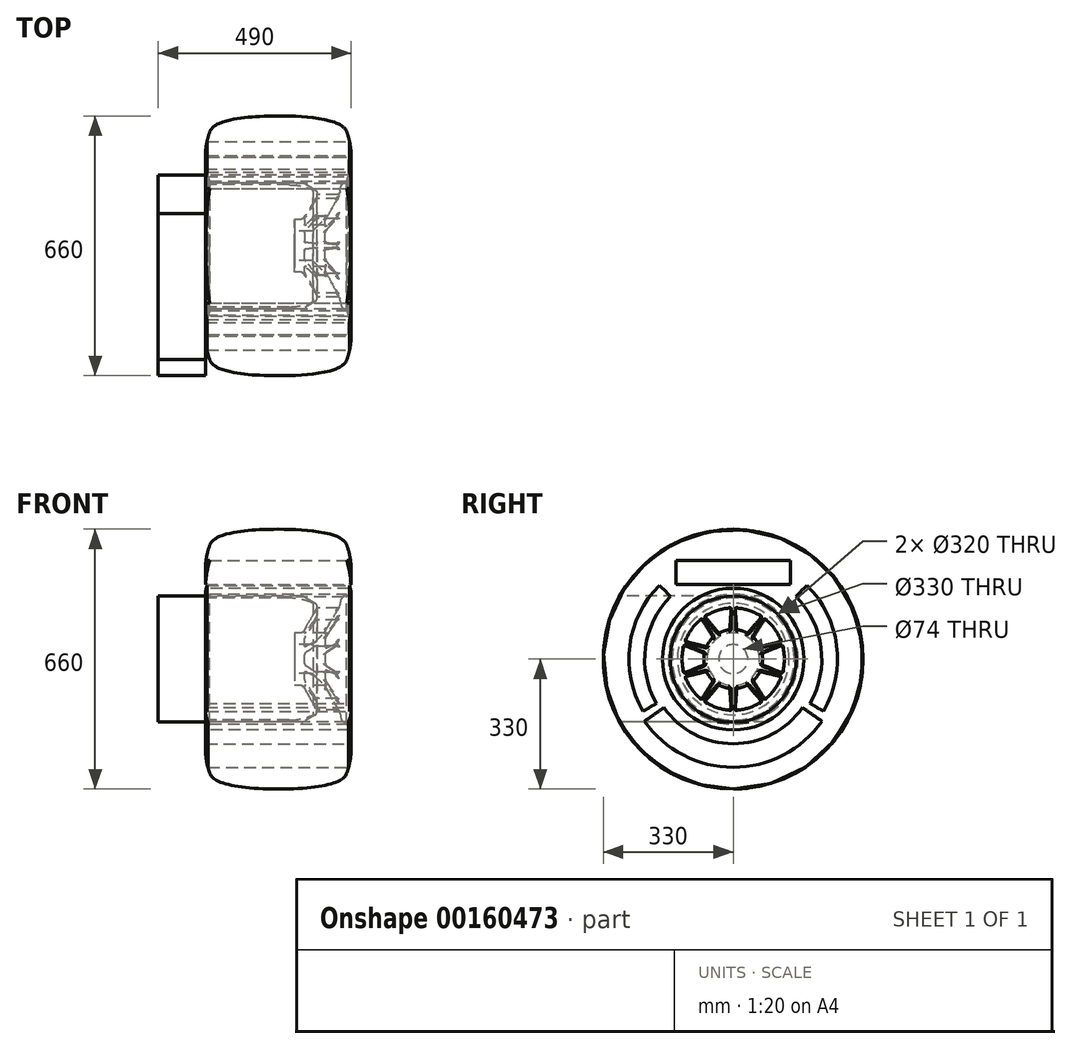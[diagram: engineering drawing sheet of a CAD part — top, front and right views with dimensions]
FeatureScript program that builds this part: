
annotation { "Feature Type Name" : "Feature", "Feature Type Description" : "" }
export const myFeature = defineFeature(function(context is Context, id is Id, definition is map)
    precondition{}
    {
        {
            var Q0;
            Q0=qCreatedBy(makeId("Front.planeOp"),FACE);
            var sketch = newSketch(context, id + "F0", { "sketchPlane" : qUnion([Q0])});
            skLineSegment(sketch, "E0.bottom", {"start": v(0, 0) * mm, "end": v(-190, 0) * mm, "construction": true});
            skLineSegment(sketch, "E0.top", {"start": v(0, 340) * mm, "end": v(-190, 340) * mm, "construction": true});
            skLineSegment(sketch, "E0.left", {"start": v(0, 0) * mm, "end": v(0, 340) * mm, "construction": true});
            skLineSegment(sketch, "E0.right", {"start": v(-190, 0) * mm, "end": v(-190, 340) * mm, "construction": true});
            skLineSegment(sketch, "E1", {"start": v(0, 165) * mm, "end": v(-174, 165) * mm});
            skEllipticalArc(sketch, "E2", {});
            skLineSegment(sketch, "E3", {"start": v(0, 330) * mm, "end": v(-190, 330) * mm, "construction": true});
            skLineSegment(sketch, "E4", {"start": v(-174, 165) * mm, "end": v(-174, 290) * mm, "construction": true});
            skEllipticalArc(sketch, "E5", {});
            skLineSegment(sketch, "E6", {"start": v(-185, 227.5) * mm, "end": v(-174, 227.5) * mm, "construction": true});
            skLineSegment(sketch, "E7.MirrorCS", {"start": v(0, 165) * mm, "end": v(174, 165) * mm});
            skEllipticalArc(sketch, "E8.MirrorCS", {});
            skEllipticalArc(sketch, "E9.MirrorCS", {});
            skLineSegment(sketch, "E10", {"start": v(-185, 227.5) * mm, "end": v(-185, 0) * mm, "construction": true});
            skLineSegment(sketch, "E11.MirrorCS", {"start": v(190, 0) * mm, "end": v(190, 340) * mm, "construction": true});
            skLineSegment(sketch, "E12.MirrorCS", {"start": v(0, 340) * mm, "end": v(190, 340) * mm, "construction": true});
            skLineSegment(sketch, "E13.MirrorCS", {"start": v(0, 0) * mm, "end": v(190, 0) * mm, "construction": true});
            const initialGuessF0  = {"E2": [0.9520342089782073, 0.02400839074373489, 0.9737164487381573, -0.22776364384324302, 1.1571666407658359, 0.15965277178562093, 2.608682838389242, 3.1257403974799214], "E5": [0.126, 0.2275, -1, 0, 0.311, 0.23709558046524198, 6.0164259862504625, 0.2667593209291309], "E8.MirrorCS": [-0.126, 0.2275, 1, 0, 0.311, 0.23709558046524198, 6.016425986250454, 0.2667593209291219], "E9.MirrorCS": [-0.9520342089782073, 0.02400839074373489, -0.9737164487381573, -0.22776364384324302, 1.1571666407658359, 0.15965277178562093, 3.1574449096996635, 3.6745024687903425]};
            skSetInitialGuess(sketch, initialGuessF0);
            skSolve(sketch);
        }
        {
            var Q0;
            Q0=qCreatedBy(makeId("Right.planeOp"),FACE);
            var sketch = newSketch(context, id + "F1", { "sketchPlane" : qUnion([Q0])});
            skLineSegment(sketch, "E14", {"start": v(0, 190) * mm, "end": v(0, -215) * mm, "construction": true});
            skLineSegment(sketch, "E15.bottom", {"start": v(0, 190) * mm, "end": v(-145, 190) * mm});
            skLineSegment(sketch, "E15.top", {"start": v(0, 250) * mm, "end": v(-145, 250) * mm});
            skLineSegment(sketch, "E15.left", {"start": v(0, 190) * mm, "end": v(0, 250) * mm});
            skLineSegment(sketch, "E15.right", {"start": v(-145, 190) * mm, "end": v(-145, 250) * mm});
            skArc(sketch, "E16", {"start": v(-159.1, 159.1) * mm, "mid": v(-223.08, 29.37) * mm, "end": v(-194.86, -112.5) * mm});
            skArc(sketch, "E17", {"start": v(-187.38, 187.38) * mm, "mid": v(-262.73, 34.59) * mm, "end": v(-229.5, -132.5) * mm});
            skLineSegment(sketch, "E18", {"start": v(-159.1, 159.1) * mm, "end": v(-187.38, 187.38) * mm});
            skLineSegment(sketch, "E19", {"start": v(-194.86, -112.5) * mm, "end": v(-229.5, -132.5) * mm});
            skArc(sketch, "E20", {"start": v(-176.12, -123.32) * mm, "mid": v(-99.28, -190.7) * mm, "end": v(0, -215) * mm});
            skArc(sketch, "E21", {"start": v(-225.27, -157.73) * mm, "mid": v(-126.98, -243.93) * mm, "end": v(0, -275) * mm});
            skLineSegment(sketch, "E22", {"start": v(-176.12, -123.32) * mm, "end": v(-225.27, -157.73) * mm});
            skLineSegment(sketch, "E23", {"start": v(0, -215) * mm, "end": v(0, -275) * mm});
            skLineSegment(sketch, "E24.MirrorCS", {"start": v(0, 250) * mm, "end": v(145, 250) * mm});
            skLineSegment(sketch, "E25.MirrorCS", {"start": v(145, 190) * mm, "end": v(145, 250) * mm});
            skLineSegment(sketch, "E26.MirrorCS", {"start": v(0, 190) * mm, "end": v(145, 190) * mm});
            skLineSegment(sketch, "E27.MirrorCS", {"start": v(159.1, 159.1) * mm, "end": v(187.38, 187.38) * mm});
            skArc(sketch, "E28.MirrorCS", {"start": v(187.38, 187.38) * mm, "mid": v(262.73, 34.59) * mm, "end": v(229.5, -132.5) * mm});
            skArc(sketch, "E29.MirrorCS", {"start": v(159.1, 159.1) * mm, "mid": v(223.08, 29.37) * mm, "end": v(194.86, -112.5) * mm});
            skLineSegment(sketch, "E30.MirrorCS", {"start": v(194.86, -112.5) * mm, "end": v(229.5, -132.5) * mm});
            skLineSegment(sketch, "E31.MirrorCS", {"start": v(176.12, -123.32) * mm, "end": v(225.27, -157.73) * mm});
            skArc(sketch, "E32.MirrorCS", {"start": v(225.27, -157.73) * mm, "mid": v(126.98, -243.93) * mm, "end": v(0, -275) * mm});
            skArc(sketch, "E33.MirrorCS", {"start": v(176.12, -123.32) * mm, "mid": v(99.28, -190.7) * mm, "end": v(0, -215) * mm});
            skSolve(sketch);
        }
        {
            var Q0;
            Q0=qCreatedBy(makeId("Front.planeOp"),FACE);
            var sketch = newSketch(context, id + "F2", { "sketchPlane" : qUnion([Q0])});
            skLineSegment(sketch, "E34.bottom", {"start": v(-180, 180) * mm, "end": v(180, 180) * mm});
            skLineSegment(sketch, "E34.top", {"start": v(-180, 160) * mm, "end": v(59.32, 160) * mm});
            skLineSegment(sketch, "E34.left", {"start": v(-185, 175) * mm, "end": v(-185, 165) * mm});
            skLineSegment(sketch, "E34.right", {"start": v(185, 175) * mm, "end": v(185, 165) * mm});
            skPoint(sketch, "E35.visualSharp", {"position": v(-185, 160) * mm});
            skArc(sketch, "E35.filletArc", {"start": v(-185, 165) * mm, "mid": v(-183.54, 161.46) * mm, "end": v(-180, 160) * mm});
            skPoint(sketch, "E36.visualSharp", {"position": v(185, 160) * mm});
            skArc(sketch, "E36.filletArc", {"start": v(180, 160) * mm, "mid": v(183.54, 161.46) * mm, "end": v(185, 165) * mm});
            skPoint(sketch, "E37.visualSharp", {"position": v(185, 180) * mm});
            skArc(sketch, "E37.filletArc", {"start": v(185, 175) * mm, "mid": v(183.54, 178.54) * mm, "end": v(180, 180) * mm});
            skPoint(sketch, "E38.visualSharp", {"position": v(-185, 180) * mm});
            skArc(sketch, "E38.filletArc", {"start": v(-180, 180) * mm, "mid": v(-183.54, 178.54) * mm, "end": v(-185, 175) * mm});
            skLineSegment(sketch, "E39", {"start": v(82.86, 37) * mm, "end": v(42, 37) * mm});
            skLineSegment(sketch, "E40", {"start": v(42, 37) * mm, "end": v(42, 67) * mm});
            skLineSegment(sketch, "E41", {"start": v(42, 67) * mm, "end": v(56.23, 67) * mm});
            skLineSegment(sketch, "E42", {"start": v(64.89, 72) * mm, "end": v(97.27, 128.09) * mm});
            skLineSegment(sketch, "E43", {"start": v(93.6, 141.75) * mm, "end": v(64.32, 158.66) * mm});
            skLineSegment(sketch, "E44", {"start": v(89.93, 39.93) * mm, "end": v(116.07, 66.07) * mm});
            skLineSegment(sketch, "E45", {"start": v(117.66, 68.14) * mm, "end": v(156.39, 135.22) * mm});
            skLineSegment(sketch, "E46", {"start": v(157.58, 138.49) * mm, "end": v(159.91, 151.74) * mm});
            skLineSegment(sketch, "E47.trimOffspring", {"start": v(169.76, 160) * mm, "end": v(180, 160) * mm});
            skPoint(sketch, "E48.visualSharp", {"position": v(62, 160) * mm});
            skArc(sketch, "E48.filletArc", {"start": v(64.32, 158.66) * mm, "mid": v(61.9, 159.66) * mm, "end": v(59.32, 160) * mm});
            skPoint(sketch, "E49.visualSharp", {"position": v(62, 67) * mm});
            skArc(sketch, "E49.filletArc", {"start": v(56.23, 67) * mm, "mid": v(61.23, 68.34) * mm, "end": v(64.89, 72) * mm});
            skPoint(sketch, "E50.visualSharp", {"position": v(87, 37) * mm});
            skArc(sketch, "E50.filletArc", {"start": v(82.86, 37) * mm, "mid": v(86.68, 37.76) * mm, "end": v(89.93, 39.93) * mm});
            skPoint(sketch, "E51.visualSharp", {"position": v(117, 67) * mm});
            skArc(sketch, "E51.filletArc", {"start": v(116.07, 66.07) * mm, "mid": v(116.93, 67.05) * mm, "end": v(117.66, 68.14) * mm});
            skPoint(sketch, "E52.visualSharp", {"position": v(157.27, 136.75) * mm});
            skArc(sketch, "E52.filletArc", {"start": v(156.39, 135.22) * mm, "mid": v(157.13, 136.8) * mm, "end": v(157.58, 138.49) * mm});
            skPoint(sketch, "E53.visualSharp", {"position": v(161.37, 160) * mm});
            skArc(sketch, "E53.filletArc", {"start": v(169.76, 160) * mm, "mid": v(163.33, 157.66) * mm, "end": v(159.91, 151.74) * mm});
            skPoint(sketch, "E54.visualSharp", {"position": v(102.27, 136.75) * mm});
            skArc(sketch, "E54.filletArc", {"start": v(97.27, 128.09) * mm, "mid": v(98.27, 135.68) * mm, "end": v(93.6, 141.75) * mm});
            skSolve(sketch);
        }
        {
            var Q0;
            Q0=qCreatedBy(makeId("Right.planeOp"),FACE);
            var sketch = newSketch(context, id + "F3", { "sketchPlane" : qUnion([Q0])});
            skLineSegment(sketch, "E55", {"start": v(5.4, 124.22) * mm, "end": v(8.6, 78.49) * mm});
            skLineSegment(sketch, "E56", {"start": v(40.17, 123.64) * mm, "end": v(23.18, 71.33) * mm, "construction": true});
            skLineSegment(sketch, "E57", {"start": v(23.18, 71.33) * mm, "end": v(0, 0) * mm, "construction": true});
            skArc(sketch, "E58", {"start": v(23.18, 71.33) * mm, "mid": v(18, 72.8) * mm, "end": v(12.73, 73.91) * mm});
            skArc(sketch, "E59", {"start": v(40.17, 123.64) * mm, "mid": v(25.66, 127.44) * mm, "end": v(10.8, 129.55) * mm});
            skArc(sketch, "E60.MirrorCS", {"start": v(23.18, 71.33) * mm, "mid": v(28.23, 69.48) * mm, "end": v(33.14, 67.28) * mm});
            skLineSegment(sketch, "E61.MirrorCS", {"start": v(68.65, 103.67) * mm, "end": v(39.18, 68.55) * mm});
            skArc(sketch, "E62.MirrorCS", {"start": v(40.17, 123.64) * mm, "mid": v(54.15, 118.18) * mm, "end": v(67.4, 111.16) * mm});
            skPoint(sketch, "E63.visualSharp", {"position": v(8.88, 74.47) * mm});
            skArc(sketch, "E63.filletArc", {"start": v(8.6, 78.49) * mm, "mid": v(9.87, 75.49) * mm, "end": v(12.73, 73.91) * mm});
            skPoint(sketch, "E64.visualSharp", {"position": v(5, 129.9) * mm});
            skArc(sketch, "E64.filletArc", {"start": v(10.8, 129.55) * mm, "mid": v(6.87, 128.13) * mm, "end": v(5.4, 124.22) * mm});
            skPoint(sketch, "E65.visualSharp", {"position": v(36.6, 65.47) * mm});
            skArc(sketch, "E65.filletArc", {"start": v(33.14, 67.28) * mm, "mid": v(36.38, 66.87) * mm, "end": v(39.18, 68.55) * mm});
            skPoint(sketch, "E66.visualSharp", {"position": v(72.31, 108.03) * mm});
            skArc(sketch, "E66.filletArc", {"start": v(68.65, 103.67) * mm, "mid": v(69.75, 107.7) * mm, "end": v(67.4, 111.16) * mm});
            skLineSegment(sketch, "E67.1.0", {"start": v(-5.4, 124.22) * mm, "end": v(-8.6, 78.49) * mm});
            skArc(sketch, "E67.1.1", {"start": v(-5.4, 124.22) * mm, "mid": v(-6.87, 128.13) * mm, "end": v(-10.8, 129.55) * mm});
            skArc(sketch, "E67.1.2", {"start": v(-40.17, 123.64) * mm, "mid": v(-25.66, 127.44) * mm, "end": v(-10.8, 129.55) * mm});
            skArc(sketch, "E67.1.3", {"start": v(-40.17, 123.64) * mm, "mid": v(-54.15, 118.18) * mm, "end": v(-67.4, 111.16) * mm});
            skArc(sketch, "E67.1.4", {"start": v(-67.4, 111.16) * mm, "mid": v(-69.75, 107.7) * mm, "end": v(-68.65, 103.67) * mm});
            skLineSegment(sketch, "E67.1.5", {"start": v(-68.65, 103.67) * mm, "end": v(-39.18, 68.55) * mm});
            skArc(sketch, "E67.1.6", {"start": v(-39.18, 68.55) * mm, "mid": v(-36.38, 66.87) * mm, "end": v(-33.14, 67.28) * mm});
            skArc(sketch, "E67.1.7", {"start": v(-23.18, 71.33) * mm, "mid": v(-28.23, 69.48) * mm, "end": v(-33.14, 67.28) * mm});
            skArc(sketch, "E67.1.8", {"start": v(-23.18, 71.33) * mm, "mid": v(-18, 72.8) * mm, "end": v(-12.73, 73.91) * mm});
            skArc(sketch, "E67.1.9", {"start": v(-12.73, 73.91) * mm, "mid": v(-9.87, 75.49) * mm, "end": v(-8.6, 78.49) * mm});
            skLineSegment(sketch, "E67.2.0", {"start": v(-77.38, 97.32) * mm, "end": v(-53.09, 58.45) * mm});
            skArc(sketch, "E67.2.1", {"start": v(-77.38, 97.32) * mm, "mid": v(-80.87, 99.62) * mm, "end": v(-84.89, 98.46) * mm});
            skArc(sketch, "E67.2.2", {"start": v(-105.17, 76.41) * mm, "mid": v(-95.67, 88.02) * mm, "end": v(-84.89, 98.46) * mm});
            skArc(sketch, "E67.2.3", {"start": v(-105.17, 76.41) * mm, "mid": v(-113.28, 63.78) * mm, "end": v(-119.87, 50.3) * mm});
            skArc(sketch, "E67.2.4", {"start": v(-119.87, 50.3) * mm, "mid": v(-119.73, 46.13) * mm, "end": v(-116.47, 43.52) * mm});
            skLineSegment(sketch, "E67.2.5", {"start": v(-116.47, 43.52) * mm, "end": v(-72, 32.43) * mm});
            skArc(sketch, "E67.2.6", {"start": v(-72, 32.43) * mm, "mid": v(-68.74, 32.72) * mm, "end": v(-66.36, 34.95) * mm});
            skArc(sketch, "E67.2.7", {"start": v(-60.68, 44.08) * mm, "mid": v(-63.68, 39.62) * mm, "end": v(-66.36, 34.95) * mm});
            skArc(sketch, "E67.2.8", {"start": v(-60.68, 44.08) * mm, "mid": v(-57.36, 48.32) * mm, "end": v(-53.75, 52.31) * mm});
            skArc(sketch, "E67.2.9", {"start": v(-53.75, 52.31) * mm, "mid": v(-52.36, 55.27) * mm, "end": v(-53.09, 58.45) * mm});
            skLineSegment(sketch, "E67.3.0", {"start": v(-119.8, 33.25) * mm, "end": v(-77.3, 16.08) * mm});
            skArc(sketch, "E67.3.1", {"start": v(-119.8, 33.25) * mm, "mid": v(-123.98, 33.06) * mm, "end": v(-126.55, 29.76) * mm});
            skArc(sketch, "E67.3.2", {"start": v(-130, 0) * mm, "mid": v(-129.13, 14.98) * mm, "end": v(-126.55, 29.76) * mm});
            skArc(sketch, "E67.3.3", {"start": v(-130, 0) * mm, "mid": v(-129.13, -14.98) * mm, "end": v(-126.55, -29.76) * mm});
            skArc(sketch, "E67.3.4", {"start": v(-126.55, -29.76) * mm, "mid": v(-123.98, -33.06) * mm, "end": v(-119.8, -33.25) * mm});
            skLineSegment(sketch, "E67.3.5", {"start": v(-119.8, -33.25) * mm, "end": v(-77.3, -16.08) * mm});
            skArc(sketch, "E67.3.6", {"start": v(-77.3, -16.08) * mm, "mid": v(-74.84, -13.94) * mm, "end": v(-74.23, -10.73) * mm});
            skArc(sketch, "E67.3.7", {"start": v(-75, 0) * mm, "mid": v(-74.8, -5.38) * mm, "end": v(-74.23, -10.73) * mm});
            skArc(sketch, "E67.3.8", {"start": v(-75, 0) * mm, "mid": v(-74.8, 5.38) * mm, "end": v(-74.23, 10.73) * mm});
            skArc(sketch, "E67.3.9", {"start": v(-74.23, 10.73) * mm, "mid": v(-74.84, 13.94) * mm, "end": v(-77.3, 16.08) * mm});
            skLineSegment(sketch, "E67.4.0", {"start": v(-116.47, -43.52) * mm, "end": v(-72, -32.43) * mm});
            skArc(sketch, "E67.4.1", {"start": v(-116.47, -43.52) * mm, "mid": v(-119.73, -46.13) * mm, "end": v(-119.87, -50.3) * mm});
            skArc(sketch, "E67.4.2", {"start": v(-105.17, -76.41) * mm, "mid": v(-113.28, -63.78) * mm, "end": v(-119.87, -50.3) * mm});
            skArc(sketch, "E67.4.3", {"start": v(-105.17, -76.41) * mm, "mid": v(-95.67, -88.02) * mm, "end": v(-84.89, -98.46) * mm});
            skArc(sketch, "E67.4.4", {"start": v(-84.89, -98.46) * mm, "mid": v(-80.87, -99.62) * mm, "end": v(-77.38, -97.32) * mm});
            skLineSegment(sketch, "E67.4.5", {"start": v(-77.38, -97.32) * mm, "end": v(-53.09, -58.45) * mm});
            skArc(sketch, "E67.4.6", {"start": v(-53.09, -58.45) * mm, "mid": v(-52.36, -55.27) * mm, "end": v(-53.75, -52.31) * mm});
            skArc(sketch, "E67.4.7", {"start": v(-60.68, -44.08) * mm, "mid": v(-57.36, -48.32) * mm, "end": v(-53.75, -52.31) * mm});
            skArc(sketch, "E67.4.8", {"start": v(-60.68, -44.08) * mm, "mid": v(-63.68, -39.62) * mm, "end": v(-66.36, -34.95) * mm});
            skArc(sketch, "E67.4.9", {"start": v(-66.36, -34.95) * mm, "mid": v(-68.74, -32.72) * mm, "end": v(-72, -32.43) * mm});
            skLineSegment(sketch, "E67.5.0", {"start": v(-68.65, -103.67) * mm, "end": v(-39.18, -68.55) * mm});
            skArc(sketch, "E67.5.1", {"start": v(-68.65, -103.67) * mm, "mid": v(-69.75, -107.7) * mm, "end": v(-67.4, -111.16) * mm});
            skArc(sketch, "E67.5.2", {"start": v(-40.17, -123.64) * mm, "mid": v(-54.15, -118.18) * mm, "end": v(-67.4, -111.16) * mm});
            skArc(sketch, "E67.5.3", {"start": v(-40.17, -123.64) * mm, "mid": v(-25.66, -127.44) * mm, "end": v(-10.8, -129.55) * mm});
            skArc(sketch, "E67.5.4", {"start": v(-10.8, -129.55) * mm, "mid": v(-6.87, -128.13) * mm, "end": v(-5.4, -124.22) * mm});
            skLineSegment(sketch, "E67.5.5", {"start": v(-5.4, -124.22) * mm, "end": v(-8.6, -78.49) * mm});
            skArc(sketch, "E67.5.6", {"start": v(-8.6, -78.49) * mm, "mid": v(-9.87, -75.49) * mm, "end": v(-12.73, -73.91) * mm});
            skArc(sketch, "E67.5.7", {"start": v(-23.18, -71.33) * mm, "mid": v(-18, -72.8) * mm, "end": v(-12.73, -73.91) * mm});
            skArc(sketch, "E67.5.8", {"start": v(-23.18, -71.33) * mm, "mid": v(-28.23, -69.48) * mm, "end": v(-33.14, -67.28) * mm});
            skArc(sketch, "E67.5.9", {"start": v(-33.14, -67.28) * mm, "mid": v(-36.38, -66.87) * mm, "end": v(-39.18, -68.55) * mm});
            skLineSegment(sketch, "E67.6.0", {"start": v(5.4, -124.22) * mm, "end": v(8.6, -78.49) * mm});
            skArc(sketch, "E67.6.1", {"start": v(5.4, -124.22) * mm, "mid": v(6.87, -128.13) * mm, "end": v(10.8, -129.55) * mm});
            skArc(sketch, "E67.6.2", {"start": v(40.17, -123.64) * mm, "mid": v(25.66, -127.44) * mm, "end": v(10.8, -129.55) * mm});
            skArc(sketch, "E67.6.3", {"start": v(40.17, -123.64) * mm, "mid": v(54.15, -118.18) * mm, "end": v(67.4, -111.16) * mm});
            skArc(sketch, "E67.6.4", {"start": v(67.4, -111.16) * mm, "mid": v(69.75, -107.7) * mm, "end": v(68.65, -103.67) * mm});
            skLineSegment(sketch, "E67.6.5", {"start": v(68.65, -103.67) * mm, "end": v(39.18, -68.55) * mm});
            skArc(sketch, "E67.6.6", {"start": v(39.18, -68.55) * mm, "mid": v(36.38, -66.87) * mm, "end": v(33.14, -67.28) * mm});
            skArc(sketch, "E67.6.7", {"start": v(23.18, -71.33) * mm, "mid": v(28.23, -69.48) * mm, "end": v(33.14, -67.28) * mm});
            skArc(sketch, "E67.6.8", {"start": v(23.18, -71.33) * mm, "mid": v(18, -72.8) * mm, "end": v(12.73, -73.91) * mm});
            skArc(sketch, "E67.6.9", {"start": v(12.73, -73.91) * mm, "mid": v(9.87, -75.49) * mm, "end": v(8.6, -78.49) * mm});
            skLineSegment(sketch, "E67.7.0", {"start": v(77.38, -97.32) * mm, "end": v(53.09, -58.45) * mm});
            skArc(sketch, "E67.7.1", {"start": v(77.38, -97.32) * mm, "mid": v(80.87, -99.62) * mm, "end": v(84.89, -98.46) * mm});
            skArc(sketch, "E67.7.2", {"start": v(105.17, -76.41) * mm, "mid": v(95.67, -88.02) * mm, "end": v(84.89, -98.46) * mm});
            skArc(sketch, "E67.7.3", {"start": v(105.17, -76.41) * mm, "mid": v(113.28, -63.78) * mm, "end": v(119.87, -50.3) * mm});
            skArc(sketch, "E67.7.4", {"start": v(119.87, -50.3) * mm, "mid": v(119.73, -46.13) * mm, "end": v(116.47, -43.52) * mm});
            skLineSegment(sketch, "E67.7.5", {"start": v(116.47, -43.52) * mm, "end": v(72, -32.43) * mm});
            skArc(sketch, "E67.7.6", {"start": v(72, -32.43) * mm, "mid": v(68.74, -32.72) * mm, "end": v(66.36, -34.95) * mm});
            skArc(sketch, "E67.7.7", {"start": v(60.68, -44.08) * mm, "mid": v(63.68, -39.62) * mm, "end": v(66.36, -34.95) * mm});
            skArc(sketch, "E67.7.8", {"start": v(60.68, -44.08) * mm, "mid": v(57.36, -48.32) * mm, "end": v(53.75, -52.31) * mm});
            skArc(sketch, "E67.7.9", {"start": v(53.75, -52.31) * mm, "mid": v(52.36, -55.27) * mm, "end": v(53.09, -58.45) * mm});
            skLineSegment(sketch, "E67.8.0", {"start": v(119.8, -33.25) * mm, "end": v(77.3, -16.08) * mm});
            skArc(sketch, "E67.8.1", {"start": v(119.8, -33.25) * mm, "mid": v(123.98, -33.06) * mm, "end": v(126.55, -29.76) * mm});
            skArc(sketch, "E67.8.2", {"start": v(130, 0) * mm, "mid": v(129.13, -14.98) * mm, "end": v(126.55, -29.76) * mm});
            skArc(sketch, "E67.8.3", {"start": v(130, 0) * mm, "mid": v(129.13, 14.98) * mm, "end": v(126.55, 29.76) * mm});
            skArc(sketch, "E67.8.4", {"start": v(126.55, 29.76) * mm, "mid": v(123.98, 33.06) * mm, "end": v(119.8, 33.25) * mm});
            skLineSegment(sketch, "E67.8.5", {"start": v(119.8, 33.25) * mm, "end": v(77.3, 16.08) * mm});
            skArc(sketch, "E67.8.6", {"start": v(77.3, 16.08) * mm, "mid": v(74.84, 13.94) * mm, "end": v(74.23, 10.73) * mm});
            skArc(sketch, "E67.8.7", {"start": v(75, 0) * mm, "mid": v(74.8, 5.38) * mm, "end": v(74.23, 10.73) * mm});
            skArc(sketch, "E67.8.8", {"start": v(75, 0) * mm, "mid": v(74.8, -5.38) * mm, "end": v(74.23, -10.73) * mm});
            skArc(sketch, "E67.8.9", {"start": v(74.23, -10.73) * mm, "mid": v(74.84, -13.94) * mm, "end": v(77.3, -16.08) * mm});
            skLineSegment(sketch, "E67.9.0", {"start": v(116.47, 43.52) * mm, "end": v(72, 32.43) * mm});
            skArc(sketch, "E67.9.1", {"start": v(116.47, 43.52) * mm, "mid": v(119.73, 46.13) * mm, "end": v(119.87, 50.3) * mm});
            skArc(sketch, "E67.9.2", {"start": v(105.17, 76.41) * mm, "mid": v(113.28, 63.78) * mm, "end": v(119.87, 50.3) * mm});
            skArc(sketch, "E67.9.3", {"start": v(105.17, 76.41) * mm, "mid": v(95.67, 88.02) * mm, "end": v(84.89, 98.46) * mm});
            skArc(sketch, "E67.9.4", {"start": v(84.89, 98.46) * mm, "mid": v(80.87, 99.62) * mm, "end": v(77.38, 97.32) * mm});
            skLineSegment(sketch, "E67.9.5", {"start": v(77.38, 97.32) * mm, "end": v(53.09, 58.45) * mm});
            skArc(sketch, "E67.9.6", {"start": v(53.09, 58.45) * mm, "mid": v(52.36, 55.27) * mm, "end": v(53.75, 52.31) * mm});
            skArc(sketch, "E67.9.7", {"start": v(60.68, 44.08) * mm, "mid": v(57.36, 48.32) * mm, "end": v(53.75, 52.31) * mm});
            skArc(sketch, "E67.9.8", {"start": v(60.68, 44.08) * mm, "mid": v(63.68, 39.62) * mm, "end": v(66.36, 34.95) * mm});
            skArc(sketch, "E67.9.9", {"start": v(66.36, 34.95) * mm, "mid": v(68.74, 32.72) * mm, "end": v(72, 32.43) * mm});
            skSolve(sketch);
        }
        {
            var Q0;
            Q0=makeQuery(id+"F0.imprint","IMPRINT",FACE,{"disambiguationData":[TD([[makeQuery(id+"F0.imprint","IMPRINT",EDGE,{"derivedFrom":sQuery(id+"F0.wireOp",EDGE,"E1")}),-1.0]])]});
            var Q1;
            Q1=sQuery(id+"F0.wireOp",EDGE,"E0.bottom");
            revolve(context, id + "F4", {"entities" : qUnion([Q0]), "axis" : qUnion([Q1]), "revolveType" : RevolveType.FULL});
        }
        {
            var Q0;
            Q0=qSketchRegion(id+"F1",true);
            var Q1;
            Q1=makeQuery(id+"F4.opRevolve","SWEPT_FACE",FACE,{"disambiguationData":[OSD([sQuery(id+"F0.wireOp",EDGE,"E5")])]});
            extrude(context, id + "F5", {"entities" : qUnion([Q0]), "endBound" : BoundingType.UP_TO_NEXT, "oppositeDirection" : true, "depth" : 25 * mm, "hasSecondDirection" : true, "secondDirectionBound" : SecondDirectionBoundingType.UP_TO_NEXT, "secondDirectionOppositeDirection" : false, "secondDirectionBoundEntityFace" : qUnion([Q1]), "secondDirectionDepth" : 25 * mm});
        }
        {
            var Q0;
            Q0=makeQuery(id+"F5.opExtrude","SWEPT_BODY",BODY,{"disambiguationData":[OSD([sQuery(id+"F1.wireOp",EDGE,"E27.MirrorCS"),sQuery(id+"F1.wireOp",EDGE,"E28.MirrorCS"),sQuery(id+"F1.wireOp",EDGE,"E29.MirrorCS"),sQuery(id+"F1.wireOp",EDGE,"E30.MirrorCS")])]});
            var Q1;
            Q1=makeQuery(id+"F5.opExtrude","SWEPT_BODY",BODY,{"disambiguationData":[OSD([sQuery(id+"F1.wireOp",EDGE,"E15.bottom"),sQuery(id+"F1.wireOp",EDGE,"E15.top"),sQuery(id+"F1.wireOp",EDGE,"E15.right"),sQuery(id+"F1.wireOp",EDGE,"E24.MirrorCS"),sQuery(id+"F1.wireOp",EDGE,"E25.MirrorCS"),sQuery(id+"F1.wireOp",EDGE,"E26.MirrorCS")])]});
            var Q2;
            Q2=makeQuery(id+"F5.opExtrude","SWEPT_BODY",BODY,{"disambiguationData":[OSD([sQuery(id+"F1.wireOp",EDGE,"E16"),sQuery(id+"F1.wireOp",EDGE,"E17"),sQuery(id+"F1.wireOp",EDGE,"E18"),sQuery(id+"F1.wireOp",EDGE,"E19")])]});
            var Q3;
            Q3=makeQuery(id+"F5.opExtrude","SWEPT_BODY",BODY,{"disambiguationData":[OSD([sQuery(id+"F1.wireOp",EDGE,"E20"),sQuery(id+"F1.wireOp",EDGE,"E21"),sQuery(id+"F1.wireOp",EDGE,"E22"),sQuery(id+"F1.wireOp",EDGE,"E31.MirrorCS"),sQuery(id+"F1.wireOp",EDGE,"E32.MirrorCS"),sQuery(id+"F1.wireOp",EDGE,"E33.MirrorCS")])]});
            var Q4;
            Q4=makeQuery(id+"F4.opRevolve","SWEPT_BODY",BODY,{"disambiguationData":[OSD([sQuery(id+"F0.wireOp",EDGE,"E1"),sQuery(id+"F0.wireOp",EDGE,"E2"),sQuery(id+"F0.wireOp",EDGE,"E5"),sQuery(id+"F0.wireOp",EDGE,"E7.MirrorCS"),sQuery(id+"F0.wireOp",EDGE,"E8.MirrorCS"),sQuery(id+"F0.wireOp",EDGE,"E9.MirrorCS")])]});
            booleanBodies(context, id + "F6", {"operationType" : BooleanOperationType.SUBTRACTION, "tools" : qUnion([Q0, Q1, Q2, Q3]), "targets" : qUnion([Q4]), "keepTools" : true});
        }
        {
            var Q0;
            Q0=qSketchRegion(id+"F2",true);
            var Q1;
            Q1=sQuery(id+"F0.wireOp",EDGE,"E13.MirrorCS");
            revolve(context, id + "F7", {"entities" : qUnion([Q0]), "axis" : qUnion([Q1]), "revolveType" : RevolveType.FULL});
        }
        {
            var Q0;
            Q0=qSketchRegion(id+"F3",true);
            extrude(context, id + "F8", {"entities" : qUnion([Q0]), "operationType" : NewBodyOperationType.REMOVE, "endBound" : BoundingType.THROUGH_ALL, "depth" : 25 * mm});
        }
        {
            var Q0;
            Q0=makeQuery(id+"F8.boolean.opBoolean","INTERSECT",EDGE,{"derivedFrom":[makeQuery(id+"F7.opRevolve","SWEPT_FACE",FACE,{"disambiguationData":[OSD([sQuery(id+"F2.wireOp",EDGE,"E45")])]}),makeQuery(id+"F8.opExtrude","SWEPT_FACE",FACE,{"disambiguationData":[OSD([sQuery(id+"F3.wireOp",EDGE,"E67.1.5")])]})]});
            var Q1;
            Q1=makeQuery(id+"F8.boolean.opBoolean","INTERSECT",EDGE,{"derivedFrom":[makeQuery(id+"F7.opRevolve","SWEPT_FACE",FACE,{"disambiguationData":[OSD([sQuery(id+"F2.wireOp",EDGE,"E45")])]}),makeQuery(id+"F8.opExtrude","SWEPT_FACE",FACE,{"disambiguationData":[OSD([sQuery(id+"F3.wireOp",EDGE,"E55")])]})]});
            var Q2;
            Q2=makeQuery(id+"F8.boolean.opBoolean","INTERSECT",EDGE,{"derivedFrom":[makeQuery(id+"F7.opRevolve","SWEPT_FACE",FACE,{"disambiguationData":[OSD([sQuery(id+"F2.wireOp",EDGE,"E45")])]}),makeQuery(id+"F8.opExtrude","SWEPT_FACE",FACE,{"disambiguationData":[OSD([sQuery(id+"F3.wireOp",EDGE,"E67.9.5")])]})]});
            var Q3;
            Q3=makeQuery(id+"F8.boolean.opBoolean","INTERSECT",EDGE,{"derivedFrom":[makeQuery(id+"F7.opRevolve","SWEPT_FACE",FACE,{"disambiguationData":[OSD([sQuery(id+"F2.wireOp",EDGE,"E45")])]}),makeQuery(id+"F8.opExtrude","SWEPT_FACE",FACE,{"disambiguationData":[OSD([sQuery(id+"F3.wireOp",EDGE,"E67.8.5")])]})]});
            var Q4;
            Q4=makeQuery(id+"F8.boolean.opBoolean","INTERSECT",EDGE,{"derivedFrom":[makeQuery(id+"F7.opRevolve","SWEPT_FACE",FACE,{"disambiguationData":[OSD([sQuery(id+"F2.wireOp",EDGE,"E45")])]}),makeQuery(id+"F8.opExtrude","SWEPT_FACE",FACE,{"disambiguationData":[OSD([sQuery(id+"F3.wireOp",EDGE,"E67.7.5")])]})]});
            var Q5;
            Q5=makeQuery(id+"F8.boolean.opBoolean","INTERSECT",EDGE,{"derivedFrom":[makeQuery(id+"F7.opRevolve","SWEPT_FACE",FACE,{"disambiguationData":[OSD([sQuery(id+"F2.wireOp",EDGE,"E45")])]}),makeQuery(id+"F8.opExtrude","SWEPT_FACE",FACE,{"disambiguationData":[OSD([sQuery(id+"F3.wireOp",EDGE,"E67.6.5")])]})]});
            var Q6;
            Q6=makeQuery(id+"F8.boolean.opBoolean","INTERSECT",EDGE,{"derivedFrom":[makeQuery(id+"F7.opRevolve","SWEPT_FACE",FACE,{"disambiguationData":[OSD([sQuery(id+"F2.wireOp",EDGE,"E45")])]}),makeQuery(id+"F8.opExtrude","SWEPT_FACE",FACE,{"disambiguationData":[OSD([sQuery(id+"F3.wireOp",EDGE,"E67.5.5")])]})]});
            var Q7;
            Q7=makeQuery(id+"F8.boolean.opBoolean","INTERSECT",EDGE,{"derivedFrom":[makeQuery(id+"F7.opRevolve","SWEPT_FACE",FACE,{"disambiguationData":[OSD([sQuery(id+"F2.wireOp",EDGE,"E45")])]}),makeQuery(id+"F8.opExtrude","SWEPT_FACE",FACE,{"disambiguationData":[OSD([sQuery(id+"F3.wireOp",EDGE,"E67.4.5")])]})]});
            var Q8;
            Q8=makeQuery(id+"F8.boolean.opBoolean","INTERSECT",EDGE,{"derivedFrom":[makeQuery(id+"F7.opRevolve","SWEPT_FACE",FACE,{"disambiguationData":[OSD([sQuery(id+"F2.wireOp",EDGE,"E45")])]}),makeQuery(id+"F8.opExtrude","SWEPT_FACE",FACE,{"disambiguationData":[OSD([sQuery(id+"F3.wireOp",EDGE,"E67.3.5")])]})]});
            var Q9;
            Q9=makeQuery(id+"F8.boolean.opBoolean","INTERSECT",EDGE,{"derivedFrom":[makeQuery(id+"F7.opRevolve","SWEPT_FACE",FACE,{"disambiguationData":[OSD([sQuery(id+"F2.wireOp",EDGE,"E45")])]}),makeQuery(id+"F8.opExtrude","SWEPT_FACE",FACE,{"disambiguationData":[OSD([sQuery(id+"F3.wireOp",EDGE,"E67.2.5")])]})]});
            fillet(context, id + "F9", {"entities" : qUnion([Q0, Q1, Q2, Q3, Q4, Q5, Q6, Q7, Q8, Q9]), "radius" : 3 * mm, "tangentPropagation" : true, "allowEdgeOverflow" : false});
        }
        {
            var Q0;
            Q0=qCreatedBy(makeId("Front.planeOp"),FACE);
            var sketch = newSketch(context, id + "F10", { "sketchPlane" : qUnion([Q0])});
            skLineSegment(sketch, "E68.bottom", {"start": v(-180, 155) * mm, "end": v(26.97, 155) * mm});
            skLineSegment(sketch, "E68.top", {"start": v(-185, 0) * mm, "end": v(88.6, 0) * mm});
            skLineSegment(sketch, "E68.left", {"start": v(-185, 150) * mm, "end": v(-185, 0) * mm});
            skLineSegment(sketch, "E68.right", {"start": v(88.6, 141.75) * mm, "end": v(88.6, 0) * mm});
            skPoint(sketch, "E69.visualSharp", {"position": v(-185, 155) * mm});
            skArc(sketch, "E69.filletArc", {"start": v(-180, 155) * mm, "mid": v(-183.54, 153.54) * mm, "end": v(-185, 150) * mm});
            skArc(sketch, "E70", {"start": v(26.97, 155) * mm, "mid": v(58.5, 151.65) * mm, "end": v(88.6, 141.75) * mm});
            skSolve(sketch);
        }
        {
            var Q0;
            Q0=qSketchRegion(id+"F10",true);
            var Q1;
            Q1=sQuery(id+"F10.wireOp",EDGE,"E68.top");
            revolve(context, id + "F11", {"entities" : qUnion([Q0]), "axis" : qUnion([Q1]), "revolveType" : RevolveType.FULL});
        }
        {
            var Q0;
            Q0=makeQuery(id+"F7.opRevolve","SWEPT_FACE",FACE,{"disambiguationData":[OSD([sQuery(id+"F2.wireOp",EDGE,"E34.left")])]});
            var sketch = newSketch(context, id + "F12", { "sketchPlane" : qUnion([Q0])});
            skLineSegment(sketch, "E71", {"start": v(-82.46, 160) * mm, "end": v(288.62, 160) * mm});
            skLineSegment(sketch, "E72", {"start": v(-180, 0) * mm, "end": v(330, 0) * mm});
            skArc(sketch, "E73", {"start": v(330, 0) * mm, "mid": v(319.49, 82.63) * mm, "end": v(288.62, 160) * mm});
            skArc(sketch, "E74.trimOffspring", {"start": v(-82.46, 160) * mm, "mid": v(-153.7, 93.7) * mm, "end": v(-180, 0) * mm});
            skArc(sketch, "E75.MirrorCS", {"start": v(-82.46, -160) * mm, "mid": v(-153.7, -93.7) * mm, "end": v(-180, 0) * mm});
            skLineSegment(sketch, "E76.MirrorCS", {"start": v(-82.46, -160) * mm, "end": v(288.62, -160) * mm});
            skArc(sketch, "E77.MirrorCS", {"start": v(330, 0) * mm, "mid": v(319.49, -82.63) * mm, "end": v(288.62, -160) * mm});
            skSolve(sketch);
        }
        {
            var Q0;
            Q0=qSketchRegion(id+"F12",true);
            extrude(context, id + "F13", {"entities" : qUnion([Q0]), "depth" : 120 * mm});
        }
    });
